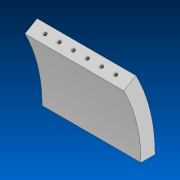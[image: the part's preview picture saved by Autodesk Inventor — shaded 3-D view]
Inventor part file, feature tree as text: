
AUTODESK INVENTOR PART (.ipt)
format: ipt  version: 2022 (Build 260153000, 153)  size: 138,752 bytes
history: native  units: in
note: dims shown in document units (in); Inventor stores cm internally (conversion verified against a paired STEP export)
features: sketch x3, hole x2, pattern_linear x2, extrude x1
ambient origin geometry x8: Origin, YZ Plane, XZ Plane, XY Plane, X Axis, Y Axis, Z Axis, Center Point
bodies: Solid1 (feature_tree)
feature tree (8):
  extrude  "Extrusion1"  TaperAngle=30.0deg  [1 undecoded]
  hole  "Hole1"  [1 undecoded]
  hole  "Hole2"  [1 undecoded]
  pattern_linear  "Rectangular Pattern1"  Spacing1=0.5in  [1 undecoded]
  pattern_linear  "Rectangular Pattern2"  Spacing1=1.0in  [1 undecoded]
  sketch  "Sketch1"  dims[d1=10.9074in d2=30.0deg]
  sketch  "Sketch2"  dims[d4=1.0in d5=1.0in]
  sketch  "Sketch3"  dims[d6=7.0in d7=0.0in d8=0.5in d9=0.5in d10=0.175in d11=0.75in d12=0.22in d13=0.325in d14=0.5635in d15=1.5in d16=0.0in d17=1.0in d18=0.5in d19=0.175in d20=0.75in d21=0.22in d22=0.325in d23=0.5635in d24=1.5in d25=0.0in d26=2.7559in d28=1.0in d29=2.3622in d31=1.0in]
note: 5 required parameter values undecoded (feature->parameter linkage not recoverable at this tier; creation-order binding heuristic only, values carry confidence <= 0.55)
